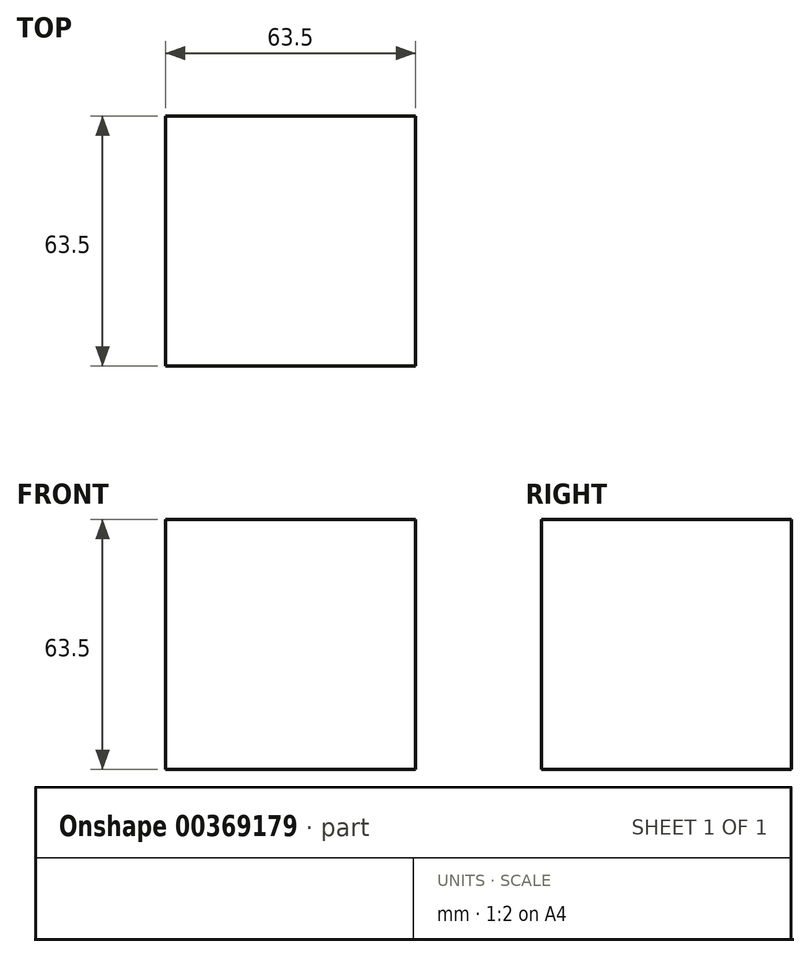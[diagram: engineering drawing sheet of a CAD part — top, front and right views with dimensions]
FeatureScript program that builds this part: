
annotation { "Feature Type Name" : "Feature", "Feature Type Description" : "" }
export const myFeature = defineFeature(function(context is Context, id is Id, definition is map)
    precondition{}
    {
        {
            var Q0;
            Q0=qCreatedBy(makeId("Front.planeOp"),FACE);
            var sketch = newSketch(context, id + "F0", { "sketchPlane" : qUnion([Q0])});
            skLineSegment(sketch, "E0.bottom", {"start": v(0, 0) * mm, "end": v(63.5, 0) * mm});
            skLineSegment(sketch, "E0.top", {"start": v(0, -63.5) * mm, "end": v(63.5, -63.5) * mm});
            skLineSegment(sketch, "E0.left", {"start": v(0, 0) * mm, "end": v(0, -63.5) * mm});
            skLineSegment(sketch, "E0.right", {"start": v(63.5, 0) * mm, "end": v(63.5, -63.5) * mm});
            skSolve(sketch);
        }
        {
            var Q0;
            Q0 = qSketchRegion(id + "F0", true);
            extrude(context, id + "F1", {"entities" : qUnion([Q0]), "depth" : 63.5 * mm});
        }
    });
